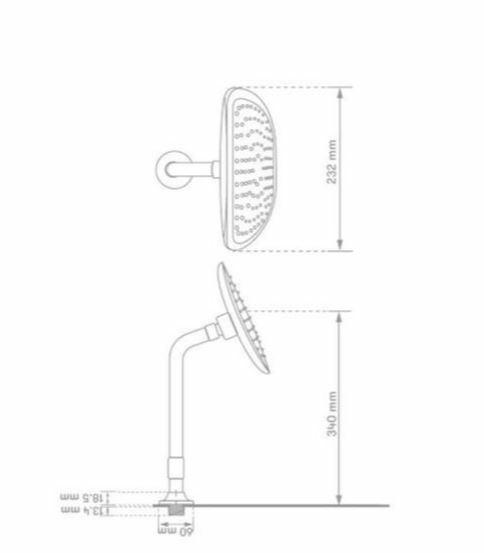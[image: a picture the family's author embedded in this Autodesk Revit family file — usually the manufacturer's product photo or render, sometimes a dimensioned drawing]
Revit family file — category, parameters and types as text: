
# Revit family: 01-2101-11 DUCHA MONOMANDO VIVALDI
name_source: partatom
category: Plumbing Fixtures
revit_build: Autodesk Revit 2018 (Build: 20170223_1515(x64)
units: mm (PartAtom-declared; Revit-internal decimal feet)

## family parameters
Cut with Voids When Loaded = No
Host = Face
OmniClass Number = 23.31.11.00
Part Type = Normal
Room Calculation Point = No
Round Connector Dimension = Use Diameter
Shared = No

## types (1)
- 01-2101-11
    Alto ducha a eje = 360 mm  [stored 1.1811 ft]
    Alto manija = 50 mm
    Ancho ducha = 230 mm  [stored 0.754593 ft]
    CW Connection = Yes
    Default Elevation = 0 mm  [stored 0 ft]
    Description = Monomando ducha
    Dim escudo ducha = 65 mm
    Dim escudo manija = 180 mm  [stored 0.590551 ft]
    HW Connection = Yes
    Link Ficha Tecnica = No encontrada en internet
    Manufacturer = Gricol
    Metal Laton Cromado = Metal Laton Cromado
    Model = 01-2101-11
    Plastico ABS Cromado = Plastico - ABS Cromado
    Product Name = DUCHA MONOMANDO VIVALDI
    Type Image = LOGO-01.jpg
    URL = https://www.gricol.com
    Vent Connection = No
    Waste Connection = No

note: [stored X ft] marks values corroborated as IEEE doubles in the binary element streams (Revit-internal decimal feet)

## geometry (parser evidence)
native form markers: Blend x2, Sweep x10
no freeform markers — native parametric forms only
